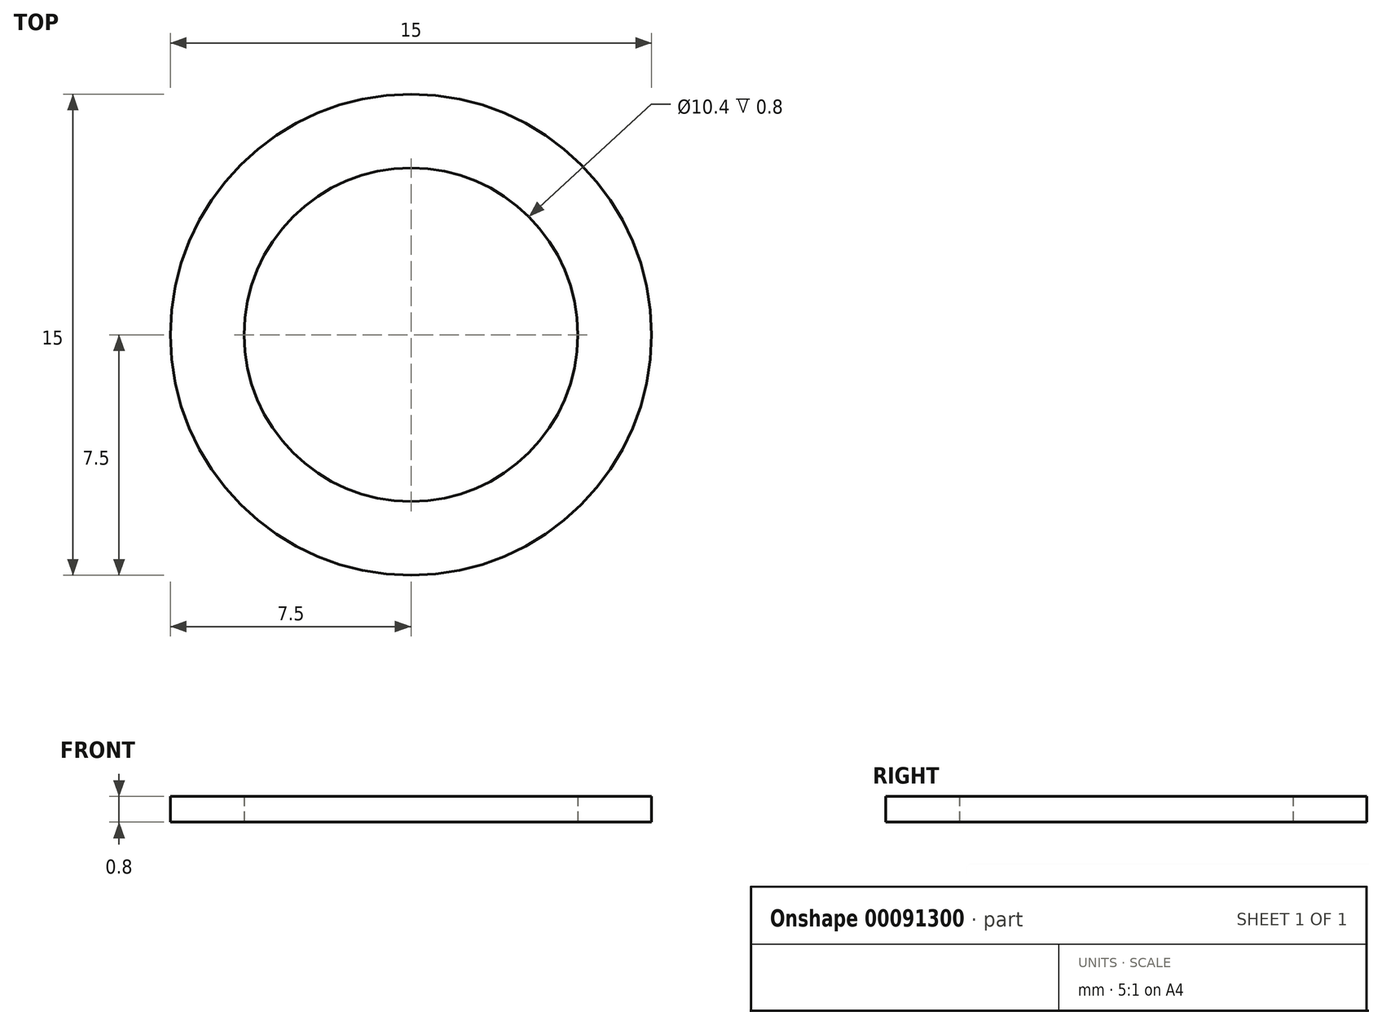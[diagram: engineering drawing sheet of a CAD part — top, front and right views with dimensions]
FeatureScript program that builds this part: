
annotation { "Feature Type Name" : "Feature", "Feature Type Description" : "" }
export const myFeature = defineFeature(function(context is Context, id is Id, definition is map)
    precondition{}
    {
        {
            var Q0;
            Q0=qCreatedBy(makeId("Top.planeOp"),FACE);
            var sketch = newSketch(context, id + "F0", { "sketchPlane" : qUnion([Q0])});
            skCircle(sketch, "E0", {"center": v(0, 0) * mm, "radius": 7.5 * mm});
            skCircle(sketch, "E1", {"center": v(0, 0) * mm, "radius": 5.2 * mm});
            skSolve(sketch);
        }
        {
            var Q0;
            Q0 = qSketchRegion(id + "F0", true);
            extrude(context, id + "F1", {"entities" : qUnion([Q0]), "flatOperationType" : FlatOperationType.REMOVE, "depth" : 0.8 * mm, "offsetDistance" : 25 * mm, "domain" : OperationDomain.MODEL});
        }
    });
